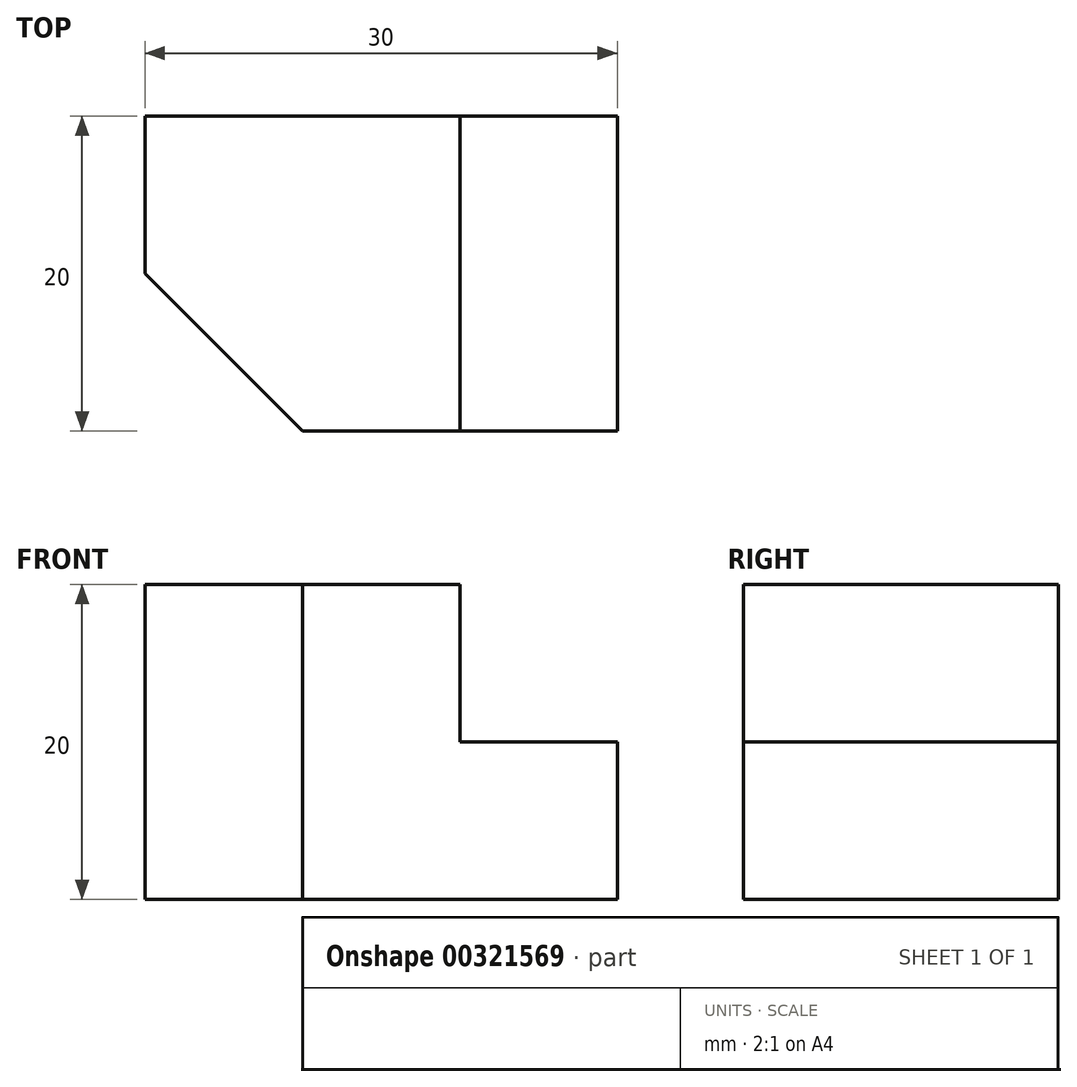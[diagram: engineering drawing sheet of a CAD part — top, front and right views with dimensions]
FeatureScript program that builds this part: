
annotation { "Feature Type Name" : "Feature", "Feature Type Description" : "" }
export const myFeature = defineFeature(function(context is Context, id is Id, definition is map)
    precondition{}
    {
        {
            var Q0;
            Q0=qCreatedBy(makeId("Front.planeOp"),FACE);
            var sketch = newSketch(context, id + "F0", { "sketchPlane" : qUnion([Q0])});
            skLineSegment(sketch, "E0.bottom", {"start": v(0, 0) * mm, "end": v(30, 0) * mm});
            skLineSegment(sketch, "E0.top", {"start": v(0, 20) * mm, "end": v(30, 20) * mm});
            skLineSegment(sketch, "E0.left", {"start": v(0, 0) * mm, "end": v(0, 20) * mm});
            skLineSegment(sketch, "E0.right", {"start": v(30, 0) * mm, "end": v(30, 20) * mm});
            skSolve(sketch);
        }
        {
            var Q0;
            Q0 = qSketchRegion(id + "F0", true);
            extrude(context, id + "F1", {"entities" : qUnion([Q0]), "depth" : 20 * mm});
        }
        {
            var Q0;
            Q0=makeQuery(id+"F1.opExtrude","CAP_FACE",FACE,{"disambiguationData":[OSD([sQuery(id+"F0.wireOp",EDGE,"E0.bottom"),sQuery(id+"F0.wireOp",EDGE,"E0.top"),sQuery(id+"F0.wireOp",EDGE,"E0.left"),sQuery(id+"F0.wireOp",EDGE,"E0.right")])],"isStart":false});
            var sketch = newSketch(context, id + "F2", { "sketchPlane" : qUnion([Q0])});
            skLineSegment(sketch, "E1.bottom", {"start": v(30, 20) * mm, "end": v(20, 20) * mm});
            skLineSegment(sketch, "E1.top", {"start": v(30, 10) * mm, "end": v(20, 10) * mm});
            skLineSegment(sketch, "E1.left", {"start": v(30, 20) * mm, "end": v(30, 10) * mm});
            skLineSegment(sketch, "E1.right", {"start": v(20, 20) * mm, "end": v(20, 10) * mm});
            skSolve(sketch);
        }
        {
            var Q0;
            Q0 = qSketchRegion(id + "F2", true);
            extrude(context, id + "F3", {"entities" : qUnion([Q0]), "operationType" : NewBodyOperationType.REMOVE, "endBound" : BoundingType.THROUGH_ALL, "oppositeDirection" : true, "depth" : 25 * mm});
        }
        {
            var Q0;
            Q0=makeQuery(id+"F1.opExtrude","SWEPT_FACE",FACE,{"disambiguationData":[OSD([sQuery(id+"F0.wireOp",EDGE,"E0.top")])]});
            var sketch = newSketch(context, id + "F4", { "sketchPlane" : qUnion([Q0])});
            skLineSegment(sketch, "E2", {"start": v(10, -20) * mm, "end": v(0, -10) * mm});
            skLineSegment(sketch, "E3", {"start": v(0, -10) * mm, "end": v(0, -20) * mm});
            skLineSegment(sketch, "E4", {"start": v(0, -20) * mm, "end": v(10, -20) * mm});
            skSolve(sketch);
        }
        {
            var Q0;
            Q0 = qSketchRegion(id + "F4", true);
            extrude(context, id + "F5", {"entities" : qUnion([Q0]), "operationType" : NewBodyOperationType.REMOVE, "endBound" : BoundingType.THROUGH_ALL, "oppositeDirection" : true, "depth" : 25 * mm});
        }
    });
